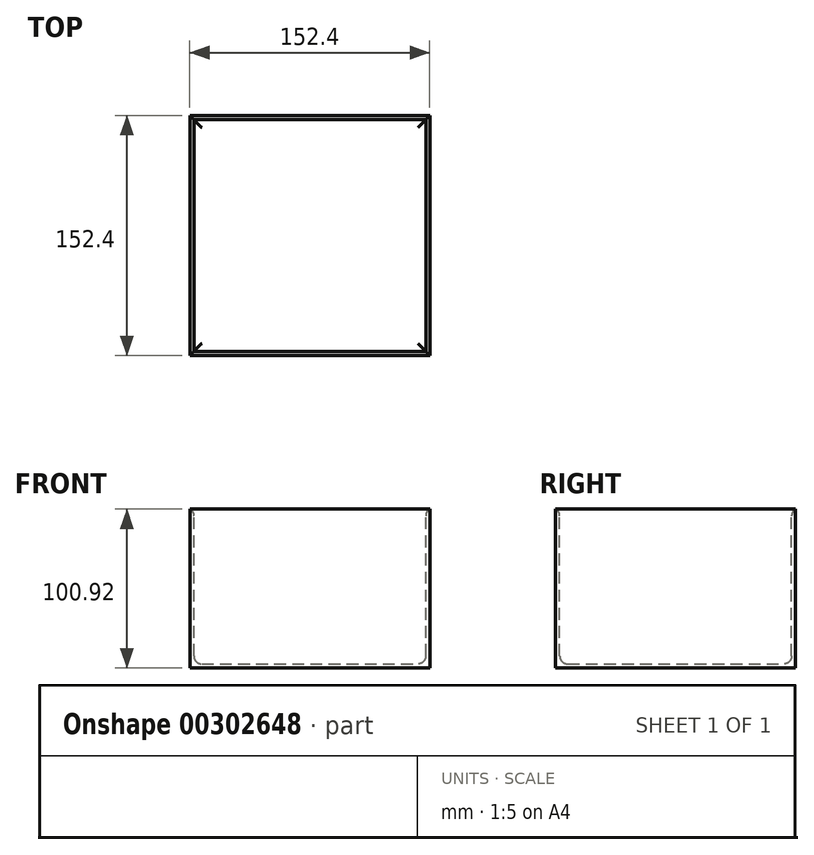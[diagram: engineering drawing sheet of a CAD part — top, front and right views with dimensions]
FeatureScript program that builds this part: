
annotation { "Feature Type Name" : "Feature", "Feature Type Description" : "" }
export const myFeature = defineFeature(function(context is Context, id is Id, definition is map)
    precondition{}
    {
        {
            var Q0;
            Q0=qCreatedBy(makeId("Front.planeOp"),FACE);
            var sketch = newSketch(context, id + "F0", { "sketchPlane" : qUnion([Q0])});
            skPoint(sketch, "E0.middle", {"position": v(0, 0) * mm});
            skLineSegment(sketch, "E1.bottom", {"start": v(-102.13, 0) * mm, "end": v(50.27, 0) * mm});
            skLineSegment(sketch, "E1.top", {"start": v(-102.13, 101.6) * mm, "end": v(50.27, 101.6) * mm});
            skLineSegment(sketch, "E1.left", {"start": v(-102.13, 0) * mm, "end": v(-102.13, 101.6) * mm});
            skLineSegment(sketch, "E1.right", {"start": v(50.27, 0) * mm, "end": v(50.27, 101.6) * mm});
            skSolve(sketch);
        }
        {
            var Q0;
            Q0=makeQuery(id+"F0.imprint","IMPRINT",FACE,{"disambiguationData":[TD([[makeQuery(id+"F0.imprint","IMPRINT",EDGE,{"derivedFrom":sQuery(id+"F0.wireOp",EDGE,"E1.bottom")}),1.0]])]});
            extrude(context, id + "F1", {"entities" : qUnion([Q0]), "depth" : 152.4 * mm});
        }
        {
            var Q0;
            Q0=makeQuery(id+"F1.opExtrude","SWEPT_FACE",FACE,{"disambiguationData":[OSD([sQuery(id+"F0.wireOp",EDGE,"E1.top")])]});
            shell(context, id + "F2", {"entities" : qUnion([Q0]), "thickness" : 2.54 * mm});
        }
        {
            var Q0;
            Q0=makeQuery(id+"F2.opShell","OFFSET_FACE",FACE,{"disambiguationData":[OSD([sQuery(id+"F0.wireOp",EDGE,"E1.bottom")])]});
            var Q1;
            {var subQ0=sQuery(id+"F0.wireOp",EDGE,"E1.top");Q1=makeQuery(id+"F2.opShell","OFFSET_EDGE",EDGE,{"disambiguationData":[OSD([subQ0]),TDD([makeQuery(id+"F1.opExtrude","CAP_EDGE",EDGE,{"disambiguationData":[OSD([subQ0])],"isStart":true})])]});}
            var Q2;
            Q2=makeQuery(id+"F2.opShell","OFFSET_EDGE",EDGE,{"disambiguationData":[OSD([sQuery(id+"F0.wireOp",EDGE,"E1.top"),sQuery(id+"F0.wireOp",EDGE,"E1.right")])]});
            var Q3;
            Q3=makeQuery(id+"F2.opShell","OFFSET_EDGE",EDGE,{"disambiguationData":[OSD([sQuery(id+"F0.wireOp",EDGE,"E1.top"),sQuery(id+"F0.wireOp",EDGE,"E1.left")])]});
            var Q4;
            {var subQ0=sQuery(id+"F0.wireOp",EDGE,"E1.top");Q4=makeQuery(id+"F2.opShell","OFFSET_EDGE",EDGE,{"disambiguationData":[OSD([subQ0]),TDD([makeQuery(id+"F1.opExtrude","CAP_EDGE",EDGE,{"disambiguationData":[OSD([subQ0])],"isStart":false})])]});}
            fillet(context, id + "F3", {"entities" : qUnion([Q0, Q1, Q2, Q3, Q4]), "radius" : 5.08 * mm, "tangentPropagation" : true, "allowEdgeOverflow" : false});
        }
    });
